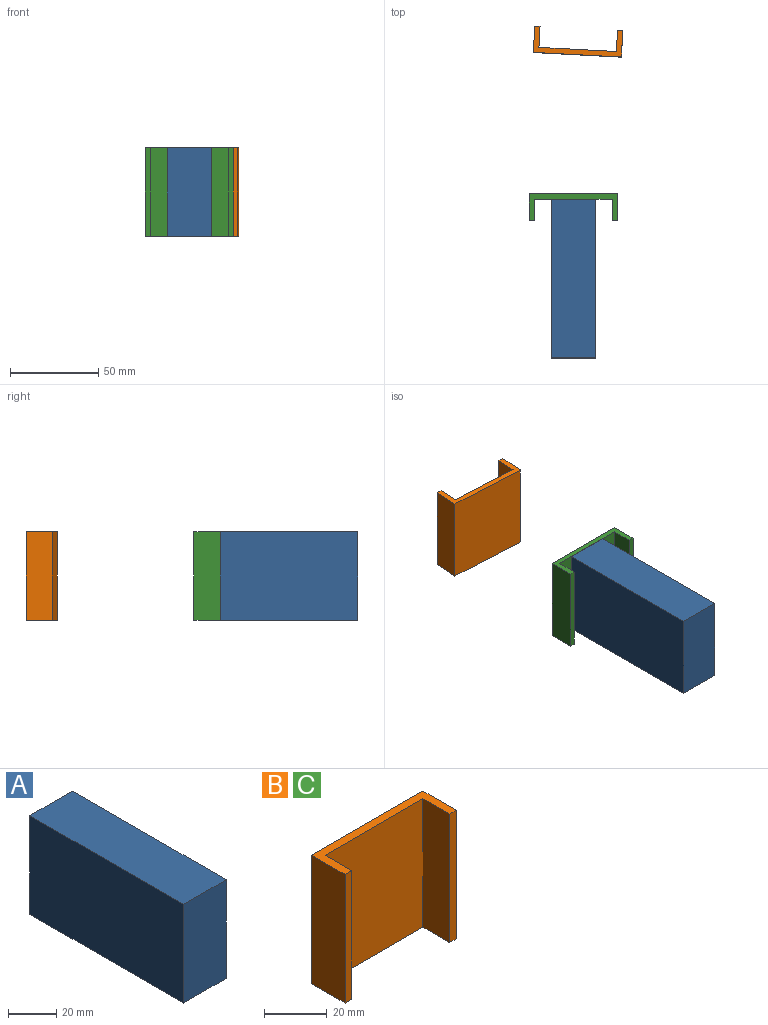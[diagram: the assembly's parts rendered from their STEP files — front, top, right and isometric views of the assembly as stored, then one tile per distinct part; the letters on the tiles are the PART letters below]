
ASSEMBLY  parts=3 mates=1
PART A: 6 faces, bbox 25x90x50 mm
  f0: plane 90x25mm, normal (0,0,-1), area 2250mm2, adj f1,f3,f4,f5
  f1: plane 50x25mm, normal (0,1,0), area 1250mm2, adj f0,f2,f4,f5
  f2: plane 90x25mm, normal (0,0,1), area 2250mm2, adj f1,f3,f4,f5
  f3: plane 50x25mm, normal (0,-1,0), area 1250mm2, adj f0,f2,f4,f5
  f4: plane 90x50mm, normal (1,0,0), area 4500mm2, adj f0,f1,f2,f3
  f5: plane 90x50mm, normal (-1,0,0), area 4500mm2, adj f0,f1,f2,f3
PART B: 10 faces, bbox 50x15x50 mm
  f0: plane 50x15mm, normal (-1,0,0), area 750mm2, adj f1,f7,f8,f9
  f1: plane 50x3mm, normal (0,-1,0), area 150mm2, adj f0,f2,f8,f9
  f2: plane 50x12mm, normal (1,0,0), area 600mm2, adj f1,f3,f8,f9
  f3: plane 50x44mm, normal (0,-1,0), area 2200mm2, adj f2,f4,f8,f9
  f4: plane 50x12mm, normal (-1,0,0), area 600mm2, adj f3,f5,f8,f9
  f5: plane 50x3mm, normal (0,-1,0), area 150mm2, adj f4,f6,f8,f9
  f6: plane 50x15mm, normal (1,0,0), area 750mm2, adj f5,f7,f8,f9
  f7: plane 50x50mm, normal (0,1,0), area 2500mm2, adj f0,f6,f8,f9
  f8: plane 50x15mm, normal (0,0,1), area 222mm2, adj f0,f1,f2,f3,f4,f5,f6,f7
  f9: plane 50x15mm, normal (0,0,-1), area 222mm2, adj f0,f1,f2,f3,f4,f5,f6,f7
PART C: same geometry as B
PLACE A t=(-12.5,-132.95,25)mm
PLACE B rot(axis=(0,0,1),177deg) t=(2.3,-6.05,0)mm
PLACE C t=(0,-84.95,0)mm
MATE fastened A.f1 <-> C.f3  axis (0,1,0) through (0,-87.95,25)mm
